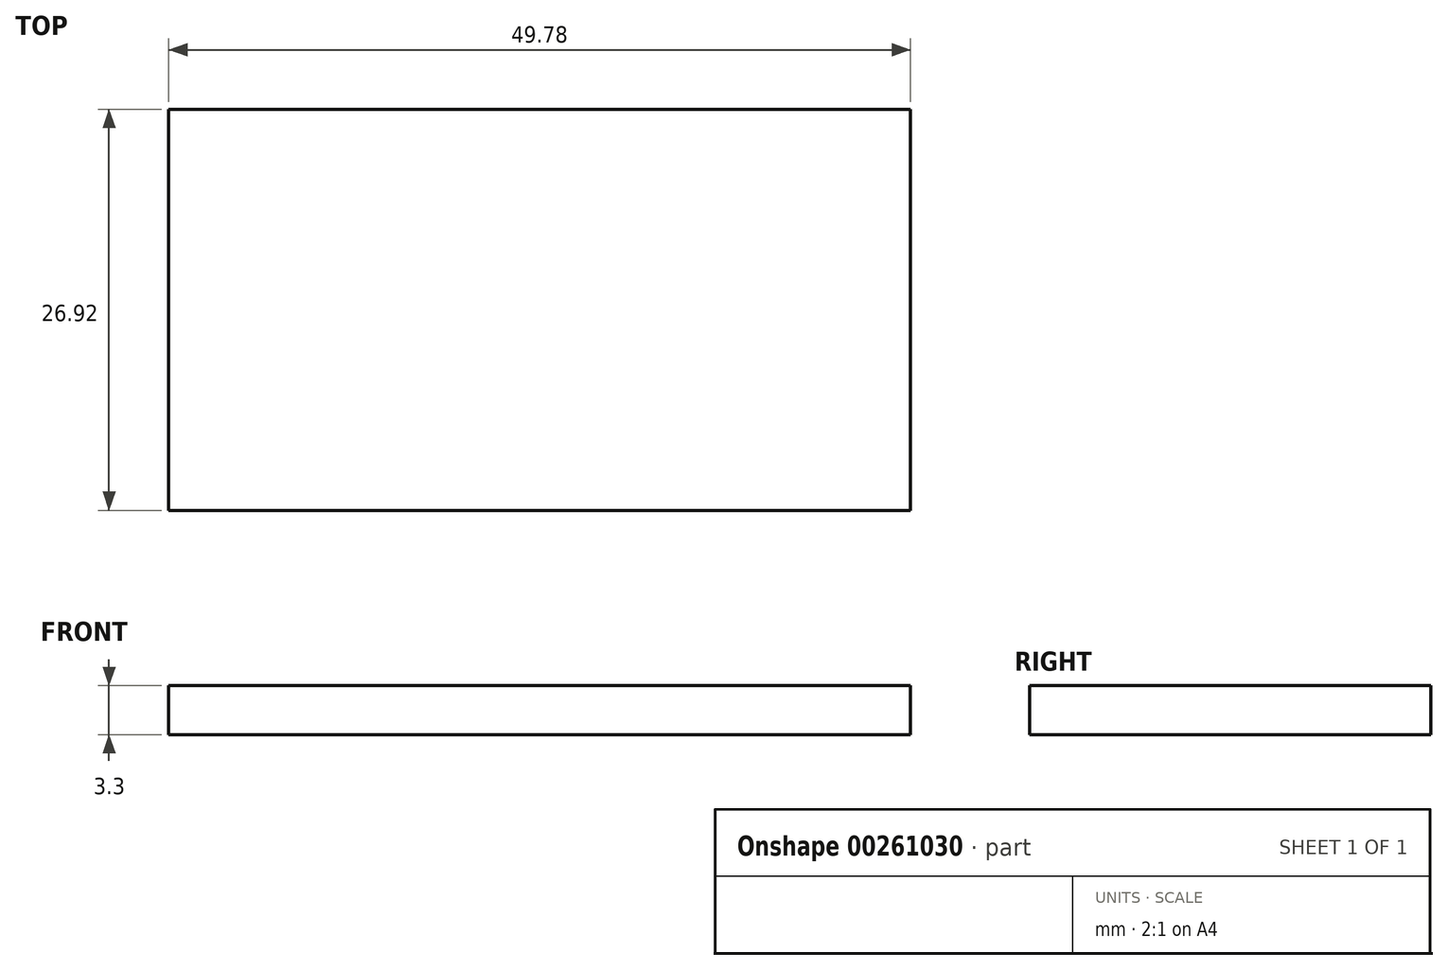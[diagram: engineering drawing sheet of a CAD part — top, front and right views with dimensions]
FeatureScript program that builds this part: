
annotation { "Feature Type Name" : "Feature", "Feature Type Description" : "" }
export const myFeature = defineFeature(function(context is Context, id is Id, definition is map)
    precondition{}
    {
        {
            var Q0;
            Q0=qCreatedBy(makeId("Top.planeOp"),FACE);
            var sketch = newSketch(context, id + "F0", { "sketchPlane" : qUnion([Q0])});
            skLineSegment(sketch, "E0.bottom", {"start": v(24.9, -13.46) * mm, "end": v(-24.9, -13.46) * mm});
            skLineSegment(sketch, "E0.top", {"start": v(24.9, 13.46) * mm, "end": v(-24.9, 13.46) * mm});
            skLineSegment(sketch, "E0.left", {"start": v(24.9, -13.46) * mm, "end": v(24.9, 13.46) * mm});
            skLineSegment(sketch, "E0.right", {"start": v(-24.9, -13.46) * mm, "end": v(-24.9, 13.46) * mm});
            skPoint(sketch, "E0.middle", {"position": v(0, 0) * mm});
            skSolve(sketch);
        }
        {
            var Q0;
            Q0 = qSketchRegion(id + "F0", true);
            extrude(context, id + "F1", {"entities" : qUnion([Q0]), "depth" : 3.3 * mm});
        }
    });
